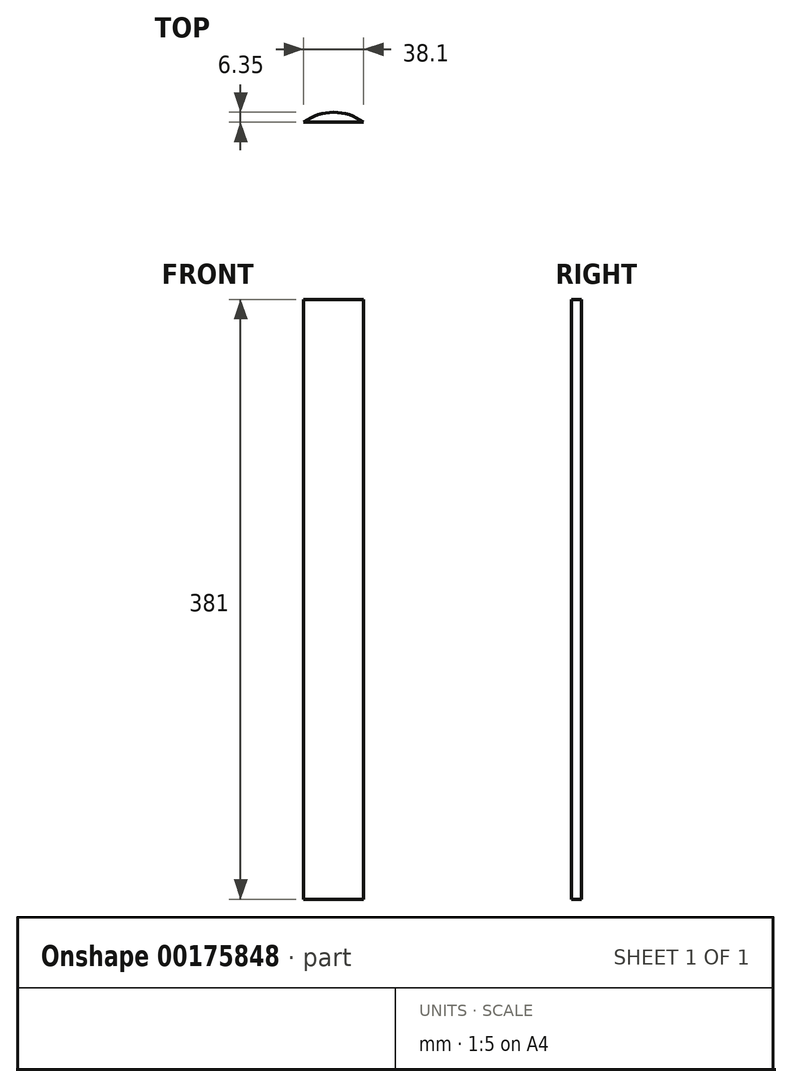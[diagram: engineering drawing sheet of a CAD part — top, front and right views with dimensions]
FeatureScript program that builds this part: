
annotation { "Feature Type Name" : "Feature", "Feature Type Description" : "" }
export const myFeature = defineFeature(function(context is Context, id is Id, definition is map)
    precondition{}
    {
        {
            var Q0;
            Q0=qCreatedBy(makeId("Top.planeOp"),FACE);
            var sketch = newSketch(context, id + "F0", { "sketchPlane" : qUnion([Q0])});
            skLineSegment(sketch, "E0.top", {"start": v(19.05, -6.35) * mm, "end": v(-19.05, -6.35) * mm});
            skPoint(sketch, "E0.middle", {"position": v(0, 0) * mm});
            skArc(sketch, "E1", {"start": v(19.05, -6.35) * mm, "mid": v(0, 0) * mm, "end": v(-19.05, -6.35) * mm});
            skSolve(sketch);
        }
        {
            var Q0;
            Q0 = qSketchRegion(id + "F0", true);
            extrude(context, id + "F1", {"entities" : qUnion([Q0]), "depth" : 381 * mm});
        }
    });
